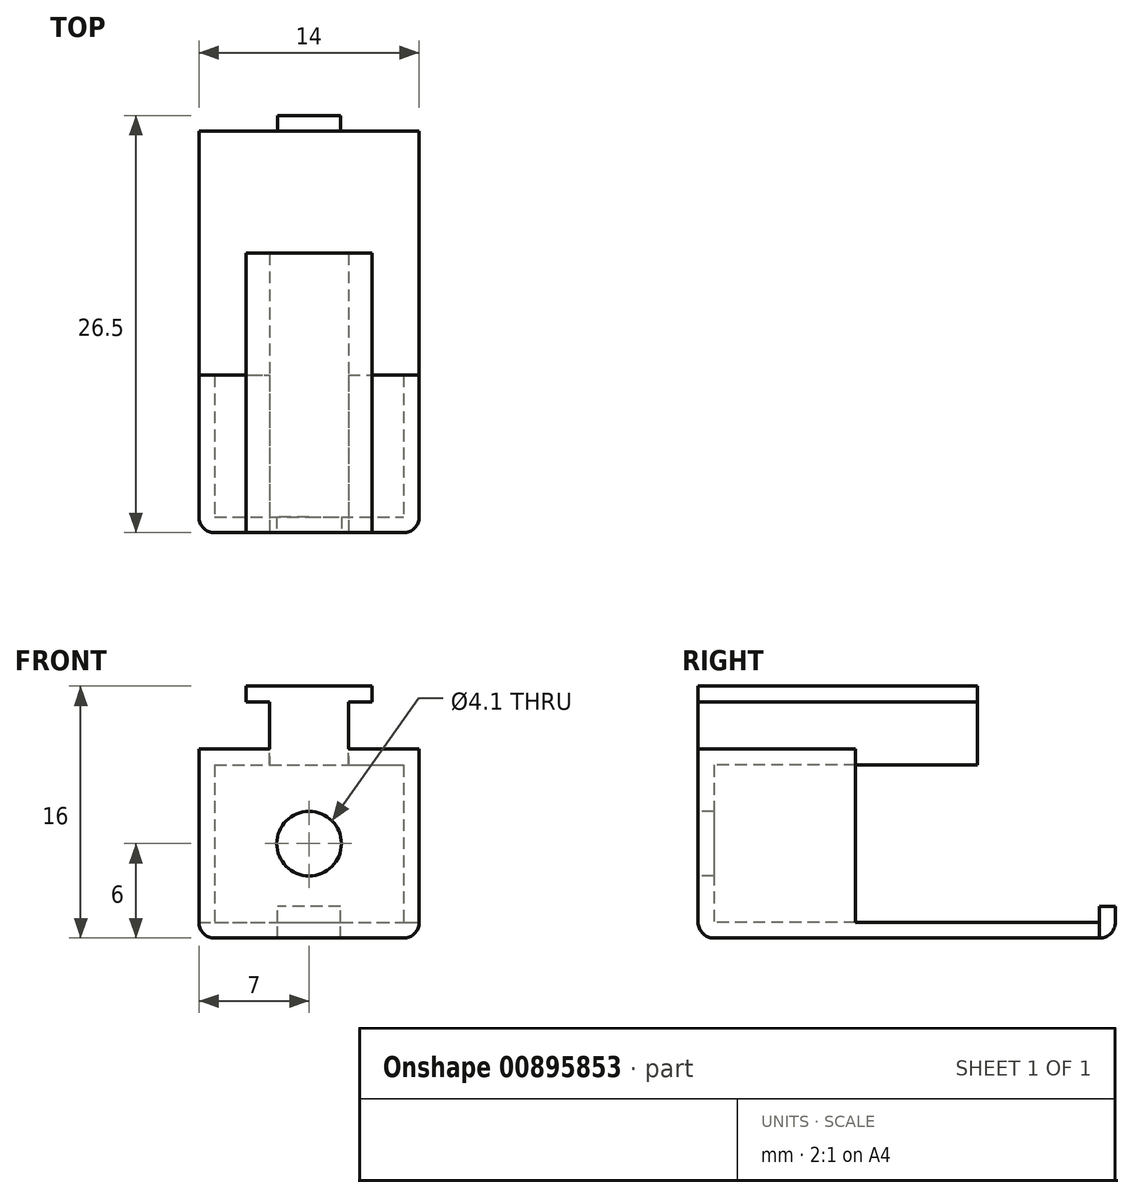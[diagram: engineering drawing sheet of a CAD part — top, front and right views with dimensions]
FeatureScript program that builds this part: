
annotation { "Feature Type Name" : "Feature", "Feature Type Description" : "" }
export const myFeature = defineFeature(function(context is Context, id is Id, definition is map)
    precondition{}
    {
        {
            var Q0;
            Q0=qCreatedBy(makeId("Top.planeOp"),FACE);
            var sketch = newSketch(context, id + "F0", { "sketchPlane" : qUnion([Q0])});
            skLineSegment(sketch, "E0.bottom", {"start": v(-7, 12.75) * mm, "end": v(7, 12.75) * mm});
            skLineSegment(sketch, "E0.top", {"start": v(-7, -12.75) * mm, "end": v(7, -12.75) * mm});
            skLineSegment(sketch, "E0.left", {"start": v(-7, 12.75) * mm, "end": v(-7, -12.75) * mm});
            skLineSegment(sketch, "E0.right", {"start": v(7, 12.75) * mm, "end": v(7, -12.75) * mm});
            skPoint(sketch, "E0.middle", {"position": v(0, 0) * mm});
            skSolve(sketch);
        }
        {
            var Q0;
            Q0 = qSketchRegion(id + "F0", true);
            extrude(context, id + "F1", {"entities" : qUnion([Q0]), "depth" : 12 * mm, "offsetDistance" : 25 * mm});
        }
        {
            var Q0;
            Q0=makeQuery(id+"F1.opExtrude","SWEPT_FACE",FACE,{"disambiguationData":[OSD([sQuery(id+"F0.wireOp",EDGE,"E0.bottom")])]});
            shell(context, id + "F2", {"entities" : qUnion([Q0]), "thickness" : 1 * mm});
        }
        {
            var Q0;
            Q0=makeQuery(id+"F1.opExtrude","SWEPT_FACE",FACE,{"disambiguationData":[OSD([sQuery(id+"F0.wireOp",EDGE,"E0.top")])]});
            var sketch = newSketch(context, id + "F3", { "sketchPlane" : qUnion([Q0])});
            skCircle(sketch, "E1", {"center": v(0, 6) * mm, "radius": 2.05 * mm});
            skPoint(sketch, "E1.centerSnap0", {"position": v(-7, 6) * mm});
            skSolve(sketch);
        }
        {
            var Q0;
            Q0 = qSketchRegion(id + "F3", true);
            extrude(context, id + "F4", {"entities" : qUnion([Q0]), "operationType" : NewBodyOperationType.REMOVE, "oppositeDirection" : true, "depth" : 25 * mm, "offsetDistance" : 25 * mm});
        }
        {
            var Q0;
            Q0=makeQuery(id+"F1.opExtrude","CAP_FACE",FACE,{"disambiguationData":[OSD([sQuery(id+"F0.wireOp",EDGE,"E0.bottom"),sQuery(id+"F0.wireOp",EDGE,"E0.top"),sQuery(id+"F0.wireOp",EDGE,"E0.left"),sQuery(id+"F0.wireOp",EDGE,"E0.right")])],"isStart":false});
            var sketch = newSketch(context, id + "F5", { "sketchPlane" : qUnion([Q0])});
            skLineSegment(sketch, "E2.bottom", {"start": v(-2.5, 5) * mm, "end": v(2.5, 5) * mm});
            skLineSegment(sketch, "E2.top", {"start": v(-2.5, -5) * mm, "end": v(2.5, -5) * mm});
            skLineSegment(sketch, "E2.left", {"start": v(-2.5, 5) * mm, "end": v(-2.5, -5) * mm});
            skLineSegment(sketch, "E2.right", {"start": v(2.5, 5) * mm, "end": v(2.5, -5) * mm});
            skPoint(sketch, "E2.middle", {"position": v(0, 0) * mm});
            skSolve(sketch);
        }
        {
            var Q0;
            Q0 = qSketchRegion(id + "F5", true);
            extrude(context, id + "F6", {"entities" : qUnion([Q0]), "operationType" : NewBodyOperationType.ADD, "depth" : 3 * mm, "offsetDistance" : 25 * mm});
        }
        {
            var Q0;
            Q0=makeQuery(id+"F1.opExtrude","CAP_EDGE",EDGE,{"disambiguationData":[OSD([sQuery(id+"F0.wireOp",EDGE,"E0.right")])],"isStart":true});
            var Q1;
            Q1=makeQuery(id+"F1.opExtrude","CAP_EDGE",EDGE,{"disambiguationData":[OSD([sQuery(id+"F0.wireOp",EDGE,"E0.left")])],"isStart":true});
            var Q2;
            Q2=makeQuery(id+"F1.opExtrude","SWEPT_EDGE",EDGE,{"disambiguationData":[OSD([sQuery(id+"F0.wireOp",EDGE,"E0.top"),sQuery(id+"F0.wireOp",EDGE,"E0.left")])]});
            var Q3;
            Q3=makeQuery(id+"F1.opExtrude","CAP_EDGE",EDGE,{"disambiguationData":[OSD([sQuery(id+"F0.wireOp",EDGE,"E0.top")])],"isStart":true});
            var Q4;
            Q4=makeQuery(id+"F1.opExtrude","SWEPT_EDGE",EDGE,{"disambiguationData":[OSD([sQuery(id+"F0.wireOp",EDGE,"E0.top"),sQuery(id+"F0.wireOp",EDGE,"E0.right")])]});
            fillet(context, id + "F7", {"entities" : qUnion([Q0, Q1, Q2, Q3, Q4]), "radius" : 1 * mm, "tangentPropagation" : true, "allowEdgeOverflow" : false});
        }
        {
            var Q0;
            Q0=makeQuery(id+"F6.opExtrude","SWEPT_FACE",FACE,{"disambiguationData":[OSD([sQuery(id+"F5.wireOp",EDGE,"E2.top")])]});
            var sketch = newSketch(context, id + "F8", { "sketchPlane" : qUnion([Q0])});
            skLineSegment(sketch, "E3.bottom", {"start": v(-2.5, 12) * mm, "end": v(2.5, 12) * mm});
            skLineSegment(sketch, "E3.top", {"start": v(-2.5, 15) * mm, "end": v(2.5, 15) * mm});
            skLineSegment(sketch, "E3.left", {"start": v(-2.5, 12) * mm, "end": v(-2.5, 15) * mm});
            skLineSegment(sketch, "E3.right", {"start": v(2.5, 12) * mm, "end": v(2.5, 15) * mm});
            skSolve(sketch);
        }
        {
            var Q0;
            Q0 = qSketchRegion(id + "F8", true);
            extrude(context, id + "F9", {"entities" : qUnion([Q0]), "operationType" : NewBodyOperationType.ADD, "depth" : 7.75 * mm, "offsetDistance" : 25 * mm});
        }
        {
            var Q0;
            Q0=makeQuery(id+"F9.boolean.opBoolean","MERGE",FACE,{"derivedFrom":[makeQuery(id+"F6.opExtrude","CAP_FACE",FACE,{"disambiguationData":[OSD([sQuery(id+"F5.wireOp",EDGE,"E2.bottom"),sQuery(id+"F5.wireOp",EDGE,"E2.top"),sQuery(id+"F5.wireOp",EDGE,"E2.left"),sQuery(id+"F5.wireOp",EDGE,"E2.right")])],"isStart":false}),makeQuery(id+"F9.opExtrude","SWEPT_FACE",FACE,{"disambiguationData":[OSD([sQuery(id+"F8.wireOp",EDGE,"E3.top")])]})]});
            var sketch = newSketch(context, id + "F10", { "sketchPlane" : qUnion([Q0])});
            skLineSegment(sketch, "E4.bottom", {"start": v(-4, 5) * mm, "end": v(4, 5) * mm});
            skLineSegment(sketch, "E4.top", {"start": v(-4, -12.75) * mm, "end": v(4, -12.75) * mm});
            skLineSegment(sketch, "E4.left", {"start": v(-4, 5) * mm, "end": v(-4, -12.75) * mm});
            skLineSegment(sketch, "E4.right", {"start": v(4, 5) * mm, "end": v(4, -12.75) * mm});
            skSolve(sketch);
        }
        {
            var Q0;
            Q0 = qSketchRegion(id + "F10", true);
            extrude(context, id + "F11", {"entities" : qUnion([Q0]), "operationType" : NewBodyOperationType.ADD, "depth" : 1 * mm, "offsetDistance" : 25 * mm});
        }
        {
            var Q0;
            Q0=makeQuery(id+"F1.opExtrude","CAP_FACE",FACE,{"disambiguationData":[OSD([sQuery(id+"F0.wireOp",EDGE,"E0.bottom"),sQuery(id+"F0.wireOp",EDGE,"E0.top"),sQuery(id+"F0.wireOp",EDGE,"E0.left"),sQuery(id+"F0.wireOp",EDGE,"E0.right")])],"isStart":false});
            var sketch = newSketch(context, id + "F12", { "sketchPlane" : qUnion([Q0])});
            skLineSegment(sketch, "E5", {"start": v(7, 12.75) * mm, "end": v(-7, 12.75) * mm});
            skLineSegment(sketch, "E6", {"start": v(-7, 12.75) * mm, "end": v(-7, -2.75) * mm});
            skLineSegment(sketch, "E7", {"start": v(-7, -2.75) * mm, "end": v(-2.5, -2.75) * mm});
            skLineSegment(sketch, "E8", {"start": v(-2.5, -2.75) * mm, "end": v(-2.5, 5) * mm});
            skLineSegment(sketch, "E9", {"start": v(-2.5, 5) * mm, "end": v(2.5, 5) * mm});
            skLineSegment(sketch, "E10", {"start": v(2.5, 5) * mm, "end": v(2.5, -2.75) * mm});
            skLineSegment(sketch, "E11", {"start": v(2.5, -2.75) * mm, "end": v(7, -2.75) * mm});
            skLineSegment(sketch, "E12", {"start": v(7, -2.75) * mm, "end": v(7, 12.75) * mm});
            skSolve(sketch);
        }
        {
            var Q0;
            Q0 = qSketchRegion(id + "F12", true);
            extrude(context, id + "F13", {"entities" : qUnion([Q0]), "operationType" : NewBodyOperationType.REMOVE, "oppositeDirection" : true, "depth" : 11 * mm, "offsetDistance" : 25 * mm});
        }
        {
            var Q0;
            Q0=makeQuery(id+"F1.opExtrude","SWEPT_FACE",FACE,{"disambiguationData":[OSD([sQuery(id+"F0.wireOp",EDGE,"E0.bottom")])]});
            var sketch = newSketch(context, id + "F14", { "sketchPlane" : qUnion([Q0])});
            skLineSegment(sketch, "E13.bottom", {"start": v(-2, 0) * mm, "end": v(2, 0) * mm});
            skLineSegment(sketch, "E13.top", {"start": v(-2, 2) * mm, "end": v(2, 2) * mm});
            skLineSegment(sketch, "E13.left", {"start": v(-2, 0) * mm, "end": v(-2, 2) * mm});
            skLineSegment(sketch, "E13.right", {"start": v(2, 0) * mm, "end": v(2, 2) * mm});
            skSolve(sketch);
        }
        {
            var Q0;
            Q0 = qSketchRegion(id + "F14", true);
            extrude(context, id + "F15", {"entities" : qUnion([Q0]), "operationType" : NewBodyOperationType.ADD, "depth" : 1 * mm, "offsetDistance" : 25 * mm});
        }
        {
            var Q0;
            Q0=makeQuery(id+"F15.opExtrude","CAP_EDGE",EDGE,{"disambiguationData":[OSD([sQuery(id+"F14.wireOp",EDGE,"E13.bottom")])],"isStart":false});
            fillet(context, id + "F16", {"entities" : qUnion([Q0]), "radius" : 1 * mm, "tangentPropagation" : true, "allowEdgeOverflow" : false});
        }
    });
